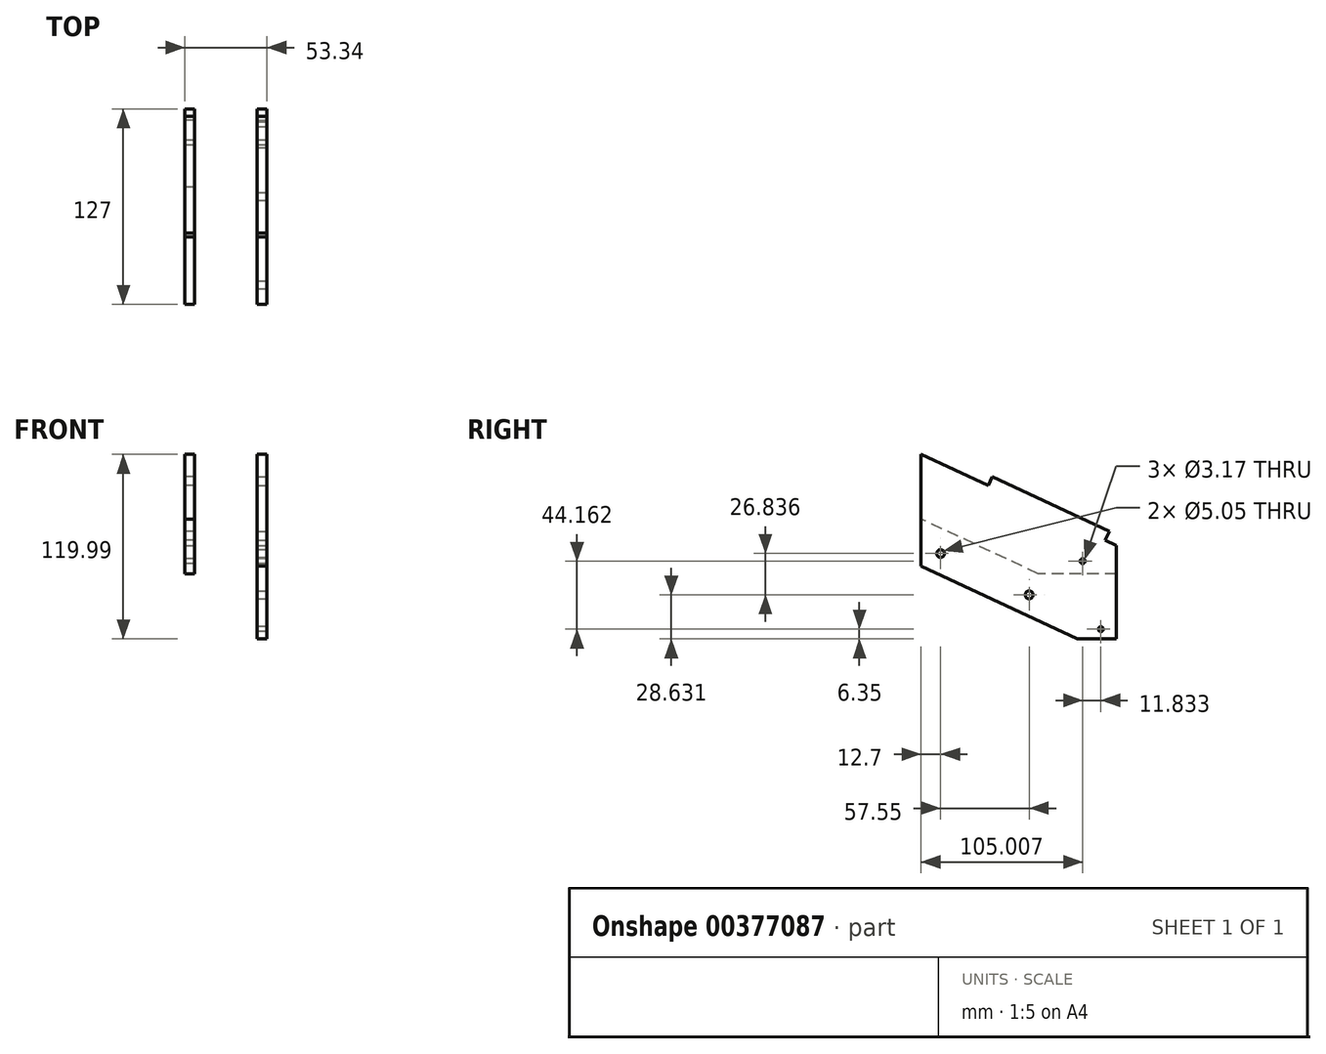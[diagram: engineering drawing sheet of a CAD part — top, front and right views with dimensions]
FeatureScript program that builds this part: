
annotation { "Feature Type Name" : "Feature", "Feature Type Description" : "" }
export const myFeature = defineFeature(function(context is Context, id is Id, definition is map)
    precondition{}
    {
        {
            var Q0;
            Q0=qCreatedBy(makeId("Right.planeOp"),FACE);
            var sketch = newSketch(context, id + "F0", { "sketchPlane" : qUnion([Q0])});
            skLineSegment(sketch, "E0.bottom", {"start": v(63.5, 4.28) * mm, "end": v(-63.5, 63.5) * mm});
            skLineSegment(sketch, "E0.top", {"start": v(63.5, -63.5) * mm, "end": v(-63.5, -63.5) * mm, "construction": true});
            skLineSegment(sketch, "E0.left", {"start": v(63.5, 4.28) * mm, "end": v(63.5, -63.5) * mm});
            skLineSegment(sketch, "E0.right", {"start": v(-63.5, 63.5) * mm, "end": v(-63.5, -63.5) * mm, "construction": true});
            skPoint(sketch, "E0.middle", {"position": v(0, 0) * mm});
            skLineSegment(sketch, "E1", {"start": v(41.5, -12.99) * mm, "end": v(53.34, -57.15) * mm, "construction": true});
            skCircle(sketch, "E2", {"center": v(41.5, -12.99) * mm, "radius": 1.59 * mm});
            skCircle(sketch, "E3", {"center": v(53.34, -57.15) * mm, "radius": 1.59 * mm});
            skLineSegment(sketch, "E4", {"start": v(-63.5, 63.5) * mm, "end": v(-63.5, -16.12) * mm});
            skLineSegment(sketch, "E5", {"start": v(-63.5, -16.12) * mm, "end": v(38.1, -63.5) * mm});
            skLineSegment(sketch, "E6", {"start": v(38.1, -63.5) * mm, "end": v(63.5, -63.5) * mm});
            skSolve(sketch);
        }
        {
            var Q0;
            Q0=qSketchRegion(id+"F0",true);
            extrude(context, id + "F1", {"entities" : qUnion([Q0]), "depth" : 6.35 * mm});
        }
        {
            var Q0;
            Q0=makeQuery(id+"F1.opExtrude","CAP_FACE",FACE,{"disambiguationData":[OSD([sQuery(id+"F0.wireOp",EDGE,"E0.bottom"),sQuery(id+"F0.wireOp",EDGE,"E0.left"),sQuery(id+"F0.wireOp",EDGE,"E2"),sQuery(id+"F0.wireOp",EDGE,"E3"),sQuery(id+"F0.wireOp",EDGE,"E4"),sQuery(id+"F0.wireOp",EDGE,"E5"),sQuery(id+"F0.wireOp",EDGE,"E6")])],"isStart":true});
            var sketch = newSketch(context, id + "F2", { "sketchPlane" : qUnion([Q0])});
            skLineSegment(sketch, "E7", {"start": v(63.5, 56.5) * mm, "end": v(11.7, 32.34) * mm});
            skLineSegment(sketch, "E8", {"start": v(11.7, 32.34) * mm, "end": v(9.02, 38.1) * mm});
            skLineSegment(sketch, "E9", {"start": v(11.7, 32.34) * mm, "end": v(-55.06, 1.2) * mm});
            skLineSegment(sketch, "E10", {"start": v(-55.06, 1.2) * mm, "end": v(-63.5, -2.73) * mm});
            skLineSegment(sketch, "E11", {"start": v(-55.06, 1.2) * mm, "end": v(-57.74, 6.96) * mm});
            skSolve(sketch);
        }
        {
            var Q0;
            Q0=qSketchRegion(id+"F2",true);
            var Q1;
            {var subQ0=sQuery(id+"F2.wireOp",EDGE,"E7");Q1=makeQuery(id+"F2.imprint","IMPRINT",FACE,{"disambiguationData":[TD([[makeQuery(id+"F2.imprint","IMPRINT",EDGE,{"derivedFrom":subQ0}),-1.0]])]});}
            var Q2;
            {var subQ0=sQuery(id+"F2.wireOp",EDGE,"E10");Q2=makeQuery(id+"F2.imprint","IMPRINT",FACE,{"disambiguationData":[TD([[makeQuery(id+"F2.imprint","IMPRINT",EDGE,{"derivedFrom":subQ0}),-1.0]])]});}
            var Q3;
            {var subQ0=sQuery(id+"F2.wireOp",EDGE,"E8");Q3=makeQuery(id+"F2.imprint","IMPRINT",FACE,{"disambiguationData":[TD([[makeQuery(id+"F2.imprint","IMPRINT",EDGE,{"derivedFrom":subQ0}),1.0]])]});}
            extrude(context, id + "F3", {"entities" : qUnion([Q0, Q1, Q2, Q3]), "operationType" : NewBodyOperationType.ADD, "depth" : 47 * mm});
        }
        {
            var Q0;
            {var subQ0=sQuery(id+"F2.wireOp",EDGE,"E8");var subQ1=sQuery(id+"F0.wireOp",EDGE,"E0.bottom");Q0=makeQuery(id+"FdCQDafgkdNC6di_1.boolean.opBoolean","MERGE",FACE,{"derivedFrom":[makeQuery(id+"F3.opExtrude","CAP_FACE",FACE,{"disambiguationData":[OSD([subQ1,sQuery(id+"F0.wireOp",EDGE,"E4"),sQuery(id+"F2.wireOp",EDGE,"E7"),subQ0])],"isStart":false}),makeQuery(id+"F3.opExtrude","CAP_FACE",FACE,{"disambiguationData":[OSD([subQ1,sQuery(id+"F0.wireOp",EDGE,"E0.left"),sQuery(id+"F2.wireOp",EDGE,"E10"),sQuery(id+"F2.wireOp",EDGE,"E11")])],"isStart":false}),makeQuery(id+"FdCQDafgkdNC6di_1.opExtrude","SWEPT_FACE",FACE,{"disambiguationData":[OSD([subQ0])]})]});}
            var sketch = newSketch(context, id + "F4", { "sketchPlane" : qUnion([Q0])});
            skLineSegment(sketch, "E12", {"start": v(-63.5, 4.28) * mm, "end": v(-63.5, -21.12) * mm});
            skLineSegment(sketch, "E13", {"start": v(-63.5, -21.12) * mm, "end": v(-12.7, -21.12) * mm});
            skLineSegment(sketch, "E14", {"start": v(-12.7, -21.12) * mm, "end": v(63.5, 14.41) * mm});
            skLineSegment(sketch, "E15", {"start": v(-63.5, 4.28) * mm, "end": v(63.5, 63.5) * mm});
            skLineSegment(sketch, "E16", {"start": v(63.5, 63.5) * mm, "end": v(63.5, 14.41) * mm});
            skCircle(sketch, "E17.0", {"center": v(-41.5, -12.99) * mm, "radius": 1.59 * mm});
            skSolve(sketch);
        }
        {
            var Q0;
            Q0=qSketchRegion(id+"F4",true);
            extrude(context, id + "F5", {"entities" : qUnion([Q0]), "operationType" : NewBodyOperationType.ADD, "oppositeDirection" : true, "depth" : 6.35 * mm});
        }
        {
            var Q0;
            {var subQ0=sQuery(id+"F0.wireOp",EDGE,"E0.bottom");Q0=makeQuery(id+"F3.boolean.opBoolean","MERGE",FACE,{"derivedFrom":[makeQuery(id+"F1.opExtrude","SWEPT_FACE",FACE,{"disambiguationData":[OSD([subQ0])]}),makeQuery(id+"F3.opExtrude","SWEPT_FACE",FACE,{"disambiguationData":[OSD([subQ0])]})]});}
            var sketch = newSketch(context, id + "F6", { "sketchPlane" : qUnion([Q0])});
            skLineSegment(sketch, "E18.bottom", {"start": v(0, 49.4) * mm, "end": v(-3.81, 49.4) * mm});
            skLineSegment(sketch, "E18.top", {"start": v(0, -26.8) * mm, "end": v(-3.8, -26.8) * mm});
            skLineSegment(sketch, "E18.left", {"start": v(0, 49.4) * mm, "end": v(0, -26.8) * mm});
            skLineSegment(sketch, "E18.right", {"start": v(-3.81, 49.4) * mm, "end": v(-3.81, -26.8) * mm});
            skLineSegment(sketch, "E19", {"start": v(-20.32, 55.74) * mm, "end": v(-20.32, -84.39) * mm, "construction": true});
            skLineSegment(sketch, "E20.MirrorCS", {"start": v(-40.64, 49.4) * mm, "end": v(-36.83, 49.4) * mm});
            skLineSegment(sketch, "E21.MirrorCS", {"start": v(-40.64, -26.8) * mm, "end": v(-36.83, -26.8) * mm});
            skLineSegment(sketch, "E22.MirrorCS", {"start": v(-36.83, 49.4) * mm, "end": v(-36.83, -26.8) * mm});
            skLineSegment(sketch, "E23.MirrorCS", {"start": v(-40.64, 49.4) * mm, "end": v(-40.64, -26.8) * mm});
            skSolve(sketch);
        }
        {
            var Q0;
            Q0=qSketchRegion(id+"F6",true);
            extrude(context, id + "F7", {"entities" : qUnion([Q0]), "operationType" : NewBodyOperationType.REMOVE, "endBound" : BoundingType.UP_TO_NEXT, "oppositeDirection" : true, "depth" : 25.4 * mm});
        }
        {
            var Q0;
            Q0=makeQuery(id+"F1.opExtrude","CAP_FACE",FACE,{"disambiguationData":[OSD([sQuery(id+"F0.wireOp",EDGE,"E0.bottom"),sQuery(id+"F0.wireOp",EDGE,"E0.left"),sQuery(id+"F0.wireOp",EDGE,"E2"),sQuery(id+"F0.wireOp",EDGE,"E3"),sQuery(id+"F0.wireOp",EDGE,"E4"),sQuery(id+"F0.wireOp",EDGE,"E5"),sQuery(id+"F0.wireOp",EDGE,"E6")])],"isStart":false});
            var sketch = newSketch(context, id + "F8", { "sketchPlane" : qUnion([Q0])});
            skCircle(sketch, "E24", {"center": v(-50.8, -8.03) * mm, "radius": 2.53 * mm});
            skCircle(sketch, "E25", {"center": v(6.75, -34.87) * mm, "radius": 2.53 * mm});
            skLineSegment(sketch, "E26", {"start": v(-50.8, -8.03) * mm, "end": v(6.75, -34.87) * mm, "construction": true});
            skSolve(sketch);
        }
        {
            var Q0;
            Q0=qSketchRegion(id+"F8",true);
            extrude(context, id + "F9", {"entities" : qUnion([Q0]), "operationType" : NewBodyOperationType.REMOVE, "endBound" : BoundingType.UP_TO_NEXT, "oppositeDirection" : true, "depth" : 25.4 * mm});
        }
        {
            var Q0;
            {var subQ0=sQuery(id+"F0.wireOp",EDGE,"E0.bottom");Q0=makeQuery(id+"F3.boolean.opBoolean","MERGE",FACE,{"derivedFrom":[makeQuery(id+"F1.opExtrude","SWEPT_FACE",FACE,{"disambiguationData":[OSD([subQ0])]}),makeQuery(id+"F3.opExtrude","SWEPT_FACE",FACE,{"disambiguationData":[OSD([subQ0])]})]});}
            var sketch = newSketch(context, id + "F10", { "sketchPlane" : qUnion([Q0])});
            skLineSegment(sketch, "E27", {"start": v(0, 49.4) * mm, "end": v(0, 50.69) * mm});
            skLineSegment(sketch, "E28", {"start": v(0, 50.69) * mm, "end": v(6.35, 50.69) * mm});
            skLineSegment(sketch, "E29", {"start": v(0, -26.8) * mm, "end": v(0, -33.18) * mm});
            skLineSegment(sketch, "E30", {"start": v(0, -33.18) * mm, "end": v(6.35, -33.18) * mm});
            skLineSegment(sketch, "E31", {"start": v(-20.32, 55.74) * mm, "end": v(-20.32, -84.39) * mm, "construction": true});
            skLineSegment(sketch, "E32.MirrorCS", {"start": v(-40.64, 49.4) * mm, "end": v(-40.64, 50.69) * mm});
            skLineSegment(sketch, "E33.MirrorCS", {"start": v(-40.64, 50.69) * mm, "end": v(-46.99, 50.69) * mm});
            skLineSegment(sketch, "E34.MirrorCS", {"start": v(-40.64, -33.18) * mm, "end": v(-46.99, -33.18) * mm});
            skLineSegment(sketch, "E35.MirrorCS", {"start": v(-40.64, -26.8) * mm, "end": v(-40.64, -33.18) * mm});
            skSolve(sketch);
        }
        {
            var Q0;
            Q0 = qSketchRegion(id + "F10", true);
            var Q1;
            Q1=makeQuery(id+"F10.imprint","IMPRINT",FACE,{"disambiguationData":[TD([[makeQuery(id+"F10.imprint","IMPRINT",EDGE,{"derivedFrom":sQuery(id+"F10.wireOp",EDGE,"E27")}),1.0]])]});
            extrude(context, id + "F11", {"entities" : qUnion([Q0, Q1]), "operationType" : NewBodyOperationType.REMOVE, "oppositeDirection" : true, "depth" : 6.35 * mm});
        }
        {
            var Q0;
            Q0=makeQuery(id+"F11.boolean.opBoolean","COPY",FACE,{"derivedFrom":makeQuery(id+"F11.opExtrude","SWEPT_FACE",FACE,{"disambiguationData":[OSD([sQuery(id+"F0.wireOp",EDGE,"E0.bottom"),sQuery(id+"F0.wireOp",EDGE,"E0.left")])]})});
            extrude(context, id + "F12", {"entities" : qUnion([Q0]), "operationType" : NewBodyOperationType.REMOVE, "endBound" : BoundingType.THROUGH_ALL, "oppositeDirection" : true, "depth" : 25.4 * mm});
        }
    });
